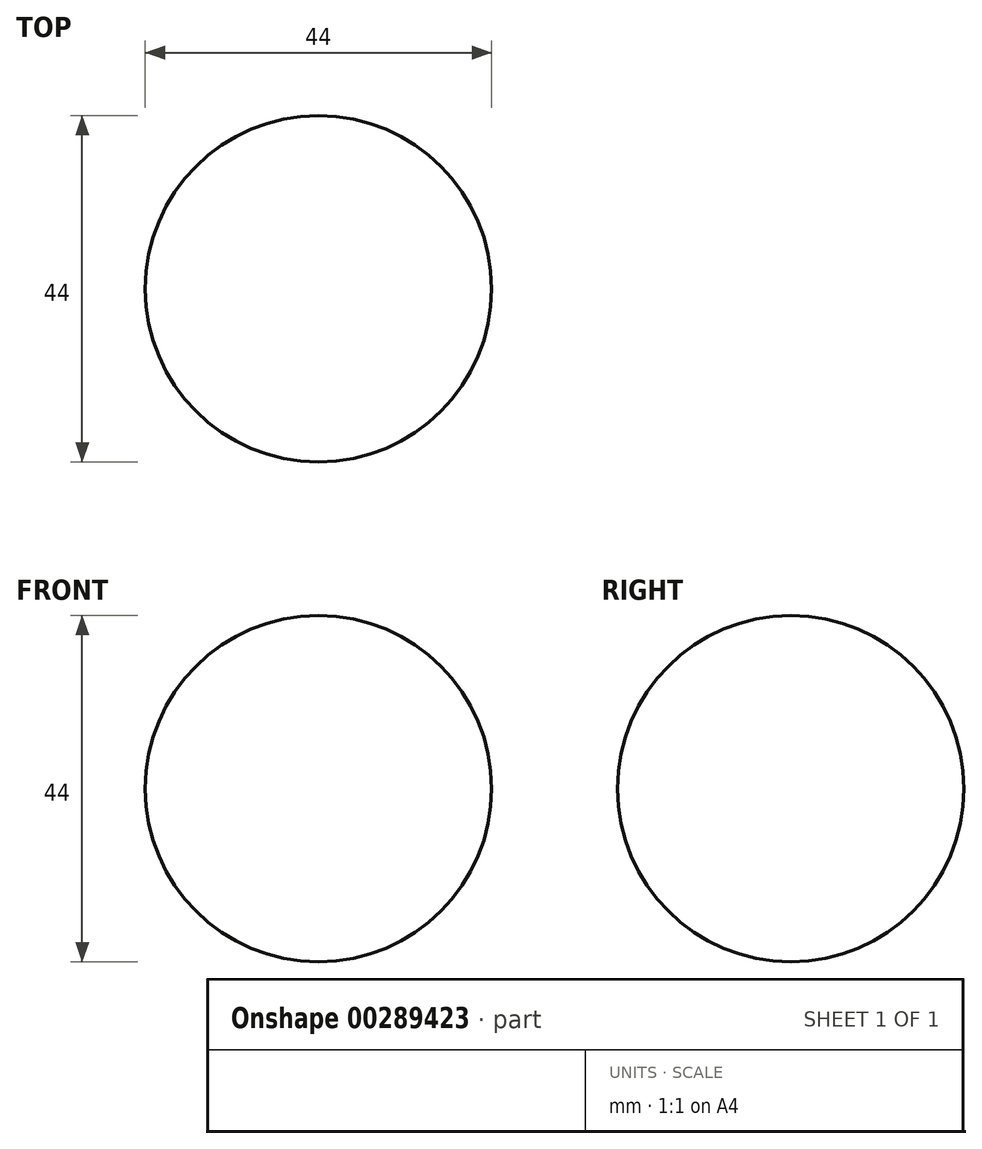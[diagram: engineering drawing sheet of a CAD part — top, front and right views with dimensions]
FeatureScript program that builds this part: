
annotation { "Feature Type Name" : "Feature", "Feature Type Description" : "" }
export const myFeature = defineFeature(function(context is Context, id is Id, definition is map)
    precondition{}
    {
        {
            var Q0;
            Q0=qCreatedBy(makeId("Top.planeOp"),FACE);
            var sketch = newSketch(context, id + "F0", { "sketchPlane" : qUnion([Q0])});
            skCircle(sketch, "E0.cCircle", {"center": v(0, 0) * mm, "radius": 12.7 * mm, "construction": true});
            skLineSegment(sketch, "E0.0", {"start": v(-22, 12.7) * mm, "end": v(22, 12.7) * mm, "construction": true});
            skLineSegment(sketch, "E0.1", {"start": v(22, 12.7) * mm, "end": v(0, -25.4) * mm, "construction": true});
            skLineSegment(sketch, "E0.2", {"start": v(0, -25.4) * mm, "end": v(-22, 12.7) * mm, "construction": true});
            skPoint(sketch, "E0.0.midPoint", {"position": v(0, 12.7) * mm});
            skCircle(sketch, "E1", {"center": v(22, 12.7) * mm, "radius": 22 * mm});
            skCircle(sketch, "E2", {"center": v(-22, 12.7) * mm, "radius": 22 * mm});
            skCircle(sketch, "E3", {"center": v(0, -25.4) * mm, "radius": 22 * mm});
            skSolve(sketch);
        }
        {
            var Q0;
            Q0=qCreatedBy(makeId("Top.planeOp"),FACE);
            var sketch = newSketch(context, id + "F1", { "sketchPlane" : qUnion([Q0])});
            skArc(sketch, "E4.0.0", {"start": v(-11, -6.35) * mm, "mid": v(0, -47.4) * mm, "end": v(11, -6.35) * mm});
            skArc(sketch, "E4.0.1", {"start": v(11, -6.35) * mm, "mid": v(0, -3.4) * mm, "end": v(-11, -6.35) * mm});
            skLineSegment(sketch, "E5", {"start": v(-22, -25.4) * mm, "end": v(22, -25.4) * mm});
            skSolve(sketch);
        }
        {
            var Q0;
            {var subQ0=sQuery(id+"F1.wireOp",EDGE,"E5");Q0=makeQuery(id+"F1.imprint","IMPRINT",FACE,{"disambiguationData":[TD([[makeQuery(id+"F1.imprint","IMPRINT",EDGE,{"derivedFrom":subQ0}),-1.0]])]});}
            var Q1;
            Q1=sQuery(id+"F1.wireOp",EDGE,"E5");
            revolve(context, id + "F2", {"entities" : qUnion([Q0]), "axis" : qUnion([Q1]), "revolveType" : RevolveType.FULL});
        }
    });
